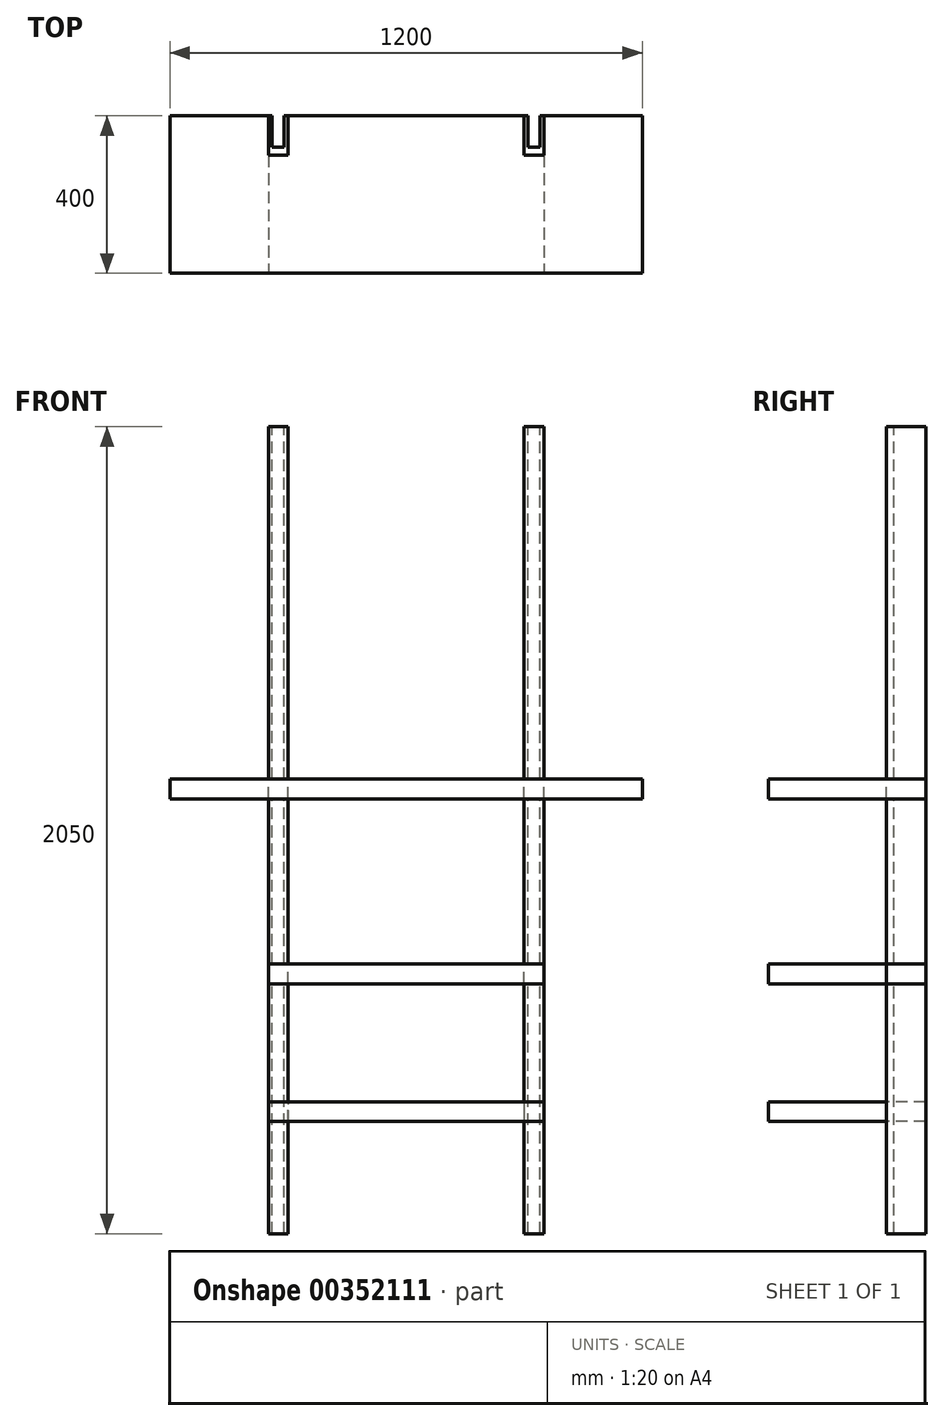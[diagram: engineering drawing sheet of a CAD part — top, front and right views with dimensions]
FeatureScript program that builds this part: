
annotation { "Feature Type Name" : "Feature", "Feature Type Description" : "" }
export const myFeature = defineFeature(function(context is Context, id is Id, definition is map)
    precondition{}
    {
        {
            var Q0;
            Q0=qCreatedBy(makeId("Top.planeOp"),FACE);
            cPlane(context, id + "F0", {"entities" : qUnion([Q0]), "cplaneType" : CPlaneType.OFFSET, "offset" : (2205 - 2050) * mm, "width" : 150 * mm, "height" : 150 * mm});
        }
        {
            var Q0;
            Q0=qCreatedBy(id+"F0.planeOp",FACE);
            var sketch = newSketch(context, id + "F1", { "sketchPlane" : qUnion([Q0])});
            skLineSegment(sketch, "E0.bottom", {"start": v(-350, 0) * mm, "end": v(-300, 0) * mm});
            skLineSegment(sketch, "E0.top", {"start": v(-350, -100) * mm, "end": v(-300, -100) * mm});
            skLineSegment(sketch, "E0.left", {"start": v(-350, 0) * mm, "end": v(-350, -100) * mm});
            skLineSegment(sketch, "E0.right", {"start": v(-300, 0) * mm, "end": v(-300, -100) * mm});
            skSolve(sketch);
        }
        {
            var Q0;
            Q0=makeQuery(id+"F1.imprint","IMPRINT",FACE,{"disambiguationData":[TD([[makeQuery(id+"F1.imprint","IMPRINT",EDGE,{"derivedFrom":sQuery(id+"F1.wireOp",EDGE,"E0.bottom")}),-1.0]])]});
            extrude(context, id + "F2", {"entities" : qUnion([Q0]), "depth" : 2050 * mm});
        }
        {
            var Q0;
            Q0=makeQuery(id+"F2.opExtrude","CAP_FACE",FACE,{"disambiguationData":[OSD([sQuery(id+"F1.wireOp",EDGE,"E0.bottom"),sQuery(id+"F1.wireOp",EDGE,"E0.top"),sQuery(id+"F1.wireOp",EDGE,"E0.left"),sQuery(id+"F1.wireOp",EDGE,"E0.right")])],"isStart":false});
            var sketch = newSketch(context, id + "F3", { "sketchPlane" : qUnion([Q0])});
            skLineSegment(sketch, "E1.bottom", {"start": v(-340, 0) * mm, "end": v(-310, 0) * mm});
            skLineSegment(sketch, "E1.top", {"start": v(-340, -80) * mm, "end": v(-310, -80) * mm});
            skLineSegment(sketch, "E1.left", {"start": v(-340, 0) * mm, "end": v(-340, -80) * mm});
            skLineSegment(sketch, "E1.right", {"start": v(-310, 0) * mm, "end": v(-310, -80) * mm});
            skLineSegment(sketch, "E2", {"start": v(-325, 0) * mm, "end": v(-325, -80) * mm, "construction": true});
            skSolve(sketch);
        }
        {
            var Q0;
            Q0=makeQuery(id+"F3.imprint","IMPRINT",FACE,{"disambiguationData":[TD([[makeQuery(id+"F3.imprint","IMPRINT",EDGE,{"derivedFrom":sQuery(id+"F3.wireOp",EDGE,"E1.bottom")}),-1.0]])]});
            extrude(context, id + "F4", {"entities" : qUnion([Q0]), "operationType" : NewBodyOperationType.REMOVE, "endBound" : BoundingType.UP_TO_NEXT, "oppositeDirection" : true, "depth" : 25 * mm});
        }
        {
            var Q0;
            Q0=makeQuery(id+"F2.opExtrude","SWEPT_BODY",BODY,{"disambiguationData":[OSD([sQuery(id+"F1.wireOp",EDGE,"E0.bottom"),sQuery(id+"F1.wireOp",EDGE,"E0.top"),sQuery(id+"F1.wireOp",EDGE,"E0.left"),sQuery(id+"F1.wireOp",EDGE,"E0.right")])]});
            var Q1;
            Q1=qCreatedBy(makeId("Right.planeOp"),FACE);
            mirror(context, id + "F5", {"entities" : qUnion([Q0]), "mirrorPlane" : qUnion([Q1])});
        }
        {
            var Q0;
            Q0=qCreatedBy(makeId("Top.planeOp"),FACE);
            cPlane(context, id + "F6", {"entities" : qUnion([Q0]), "cplaneType" : CPlaneType.OFFSET, "offset" : (1010 + 250) * mm, "width" : 150 * mm, "height" : 150 * mm});
        }
        {
            var Q0;
            Q0=qCreatedBy(id+"F6.planeOp",FACE);
            var sketch = newSketch(context, id + "F7", { "sketchPlane" : qUnion([Q0])});
            skLineSegment(sketch, "E3.bottom", {"start": v(-600, 0) * mm, "end": v(600, 0) * mm});
            skLineSegment(sketch, "E3.top", {"start": v(-600, -400) * mm, "end": v(600, -400) * mm});
            skLineSegment(sketch, "E3.left", {"start": v(-600, 0) * mm, "end": v(-600, -400) * mm});
            skLineSegment(sketch, "E3.right", {"start": v(600, 0) * mm, "end": v(600, -400) * mm});
            skLineSegment(sketch, "E4", {"start": v(0, 0) * mm, "end": v(0, -400) * mm, "construction": true});
            skSolve(sketch);
        }
        {
            var Q0;
            Q0 = qSketchRegion(id + "F7", true);
            extrude(context, id + "F8", {"entities" : qUnion([Q0]), "depth" : 50 * mm});
        }
        {
            var Q0;
            Q0=makeQuery(id+"F8.opExtrude","CAP_FACE",FACE,{"disambiguationData":[OSD([sQuery(id+"F7.wireOp",EDGE,"E3.bottom"),sQuery(id+"F7.wireOp",EDGE,"E3.top"),sQuery(id+"F7.wireOp",EDGE,"E3.left"),sQuery(id+"F7.wireOp",EDGE,"E3.right")])],"isStart":false});
            var sketch = newSketch(context, id + "F9", { "sketchPlane" : qUnion([Q0])});
            skLineSegment(sketch, "E5.bottom", {"start": v(-350, 0) * mm, "end": v(-300, 0) * mm});
            skLineSegment(sketch, "E5.top", {"start": v(-350, -100) * mm, "end": v(-300, -100) * mm});
            skLineSegment(sketch, "E5.left", {"start": v(-350, 0) * mm, "end": v(-350, -100) * mm});
            skLineSegment(sketch, "E5.right", {"start": v(-300, 0) * mm, "end": v(-300, -100) * mm});
            skLineSegment(sketch, "E6.MirrorCS", {"start": v(350, -100) * mm, "end": v(300, -100) * mm});
            skLineSegment(sketch, "E7.MirrorCS", {"start": v(300, 0) * mm, "end": v(300, -100) * mm});
            skLineSegment(sketch, "E8.MirrorCS", {"start": v(350, 0) * mm, "end": v(350, -100) * mm});
            skLineSegment(sketch, "E9.MirrorCS", {"start": v(350, 0) * mm, "end": v(300, 0) * mm});
            skSolve(sketch);
        }
        {
            var Q0;
            Q0 = qSketchRegion(id + "F9", true);
            var Q1;
            Q1=makeQuery(id+"F8.opExtrude","CAP_FACE",FACE,{"disambiguationData":[OSD([sQuery(id+"F7.wireOp",EDGE,"E3.bottom"),sQuery(id+"F7.wireOp",EDGE,"E3.top"),sQuery(id+"F7.wireOp",EDGE,"E3.left"),sQuery(id+"F7.wireOp",EDGE,"E3.right")])],"isStart":true});
            extrude(context, id + "F10", {"entities" : qUnion([Q0]), "operationType" : NewBodyOperationType.REMOVE, "endBound" : BoundingType.UP_TO_SURFACE, "oppositeDirection" : true, "endBoundEntityFace" : qUnion([Q1]), "depth" : 25 * mm});
        }
        {
            var Q0;
            Q0=qCreatedBy(makeId("Top.planeOp"),FACE);
            cPlane(context, id + "F11", {"entities" : qUnion([Q0]), "cplaneType" : CPlaneType.OFFSET, "offset" : 790 * mm, "width" : 150 * mm, "height" : 150 * mm});
        }
        {
            var Q0;
            Q0=qCreatedBy(id+"F11.planeOp",FACE);
            var sketch = newSketch(context, id + "F12", { "sketchPlane" : qUnion([Q0])});
            skLineSegment(sketch, "E10.bottom", {"start": v(-350, 0) * mm, "end": v(350, 0) * mm});
            skLineSegment(sketch, "E10.top", {"start": v(-350, -400) * mm, "end": v(350, -400) * mm});
            skLineSegment(sketch, "E10.left", {"start": v(-350, 0) * mm, "end": v(-350, -400) * mm});
            skLineSegment(sketch, "E10.right", {"start": v(350, 0) * mm, "end": v(350, -400) * mm});
            skSolve(sketch);
        }
        {
            var Q0;
            Q0=makeQuery(id+"F12.imprint","IMPRINT",FACE,{"disambiguationData":[TD([[makeQuery(id+"F12.imprint","IMPRINT",EDGE,{"derivedFrom":sQuery(id+"F12.wireOp",EDGE,"E10.bottom")}),-1.0]])]});
            extrude(context, id + "F13", {"entities" : qUnion([Q0]), "depth" : 50 * mm});
        }
        {
            var Q0;
            Q0=makeQuery(id+"F13.opExtrude","CAP_FACE",FACE,{"disambiguationData":[OSD([sQuery(id+"F12.wireOp",EDGE,"E10.bottom"),sQuery(id+"F12.wireOp",EDGE,"E10.top"),sQuery(id+"F12.wireOp",EDGE,"E10.left"),sQuery(id+"F12.wireOp",EDGE,"E10.right")])],"isStart":false});
            var sketch = newSketch(context, id + "F14", { "sketchPlane" : qUnion([Q0])});
            skLineSegment(sketch, "E11.bottom", {"start": v(-350, -100) * mm, "end": v(-300, -100) * mm});
            skLineSegment(sketch, "E11.top", {"start": v(-350, 0) * mm, "end": v(-300, 0) * mm});
            skLineSegment(sketch, "E11.left", {"start": v(-350, -100) * mm, "end": v(-350, 0) * mm});
            skLineSegment(sketch, "E11.right", {"start": v(-300, -100) * mm, "end": v(-300, 0) * mm});
            skLineSegment(sketch, "E12.bottom", {"start": v(300, 0) * mm, "end": v(350, 0) * mm});
            skLineSegment(sketch, "E12.top", {"start": v(300, -100) * mm, "end": v(350, -100) * mm});
            skLineSegment(sketch, "E12.left", {"start": v(300, 0) * mm, "end": v(300, -100) * mm});
            skLineSegment(sketch, "E12.right", {"start": v(350, 0) * mm, "end": v(350, -100) * mm});
            skSolve(sketch);
        }
        {
            var Q0;
            Q0 = qSketchRegion(id + "F14", true);
            extrude(context, id + "F15", {"entities" : qUnion([Q0]), "operationType" : NewBodyOperationType.REMOVE, "endBound" : BoundingType.UP_TO_NEXT, "oppositeDirection" : true, "depth" : 25 * mm});
        }
        {
            var Q0;
            Q0=makeQuery(id+"F13.opExtrude","SWEPT_BODY",BODY,{"disambiguationData":[OSD([sQuery(id+"F12.wireOp",EDGE,"E10.bottom"),sQuery(id+"F12.wireOp",EDGE,"E10.top"),sQuery(id+"F12.wireOp",EDGE,"E10.left"),sQuery(id+"F12.wireOp",EDGE,"E10.right")])]});
            transform(context, id + "F16", {"entities" : qUnion([Q0]), "transformType" : TransformType.TRANSLATION_3D, "dx" : 0 * mm, "dy" : 0 * mm, "dz" : -350 * mm, "makeCopy" : true});
        }
    });
